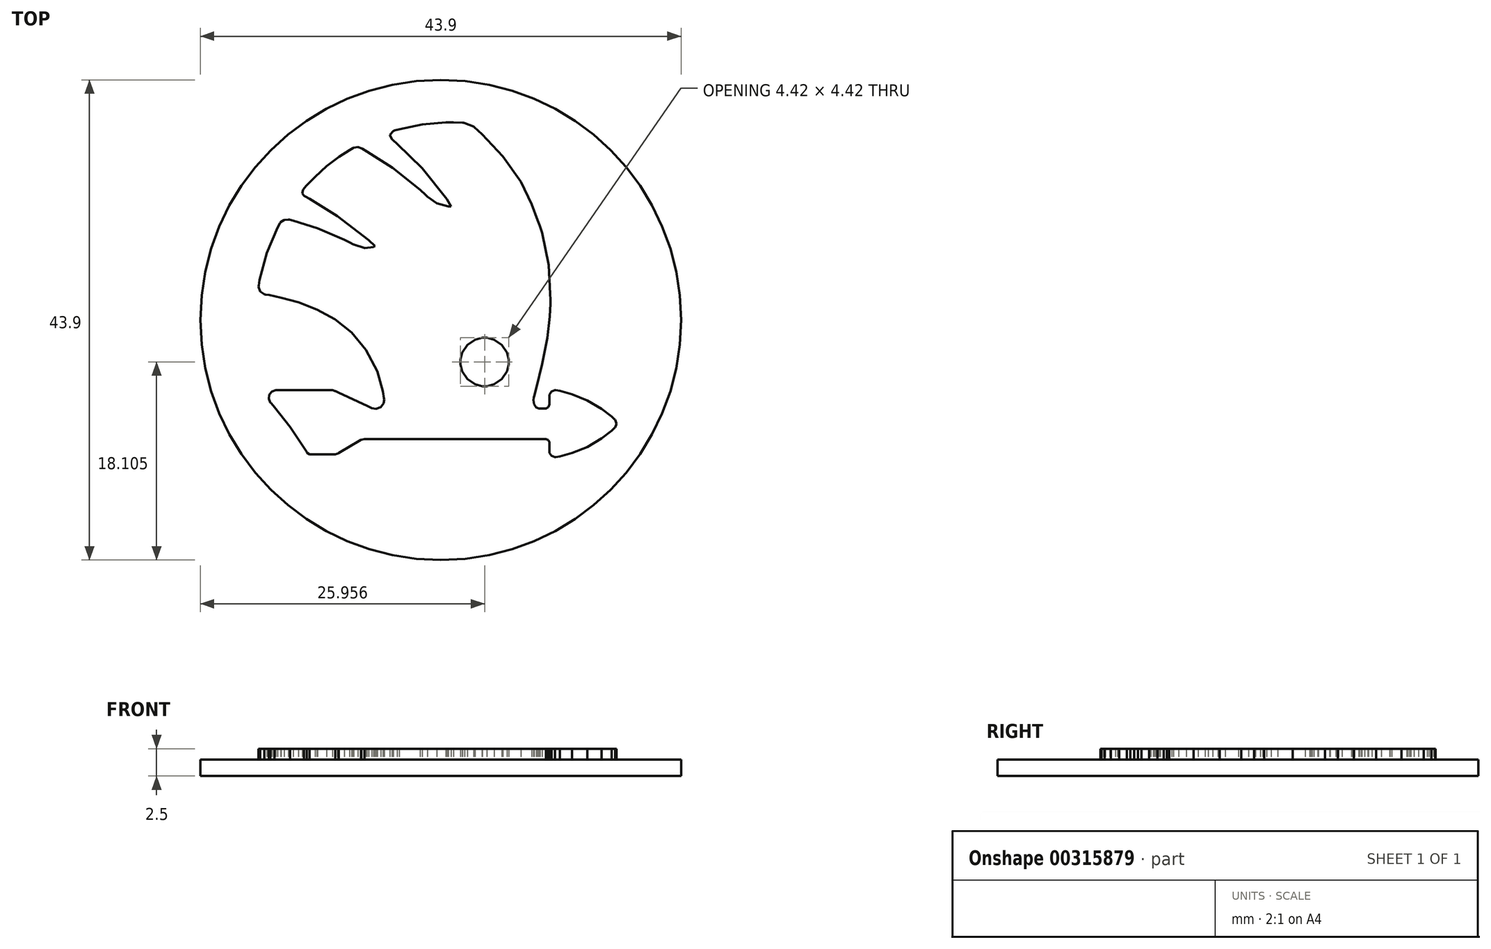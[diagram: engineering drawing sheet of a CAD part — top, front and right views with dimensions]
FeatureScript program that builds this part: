
annotation { "Feature Type Name" : "Feature", "Feature Type Description" : "" }
export const myFeature = defineFeature(function(context is Context, id is Id, definition is map)
    precondition{}
    {
        {
            var Q0;
            Q0=qCreatedBy(makeId("Top.planeOp"),FACE);
            var sketch = newSketch(context, id + "F0", { "sketchPlane" : qUnion([Q0])});
            skCircle(sketch, "E0", {"center": v(0, 0) * mm, "radius": 21.95 * mm});
            skLineSegment(sketch, "E1", {"start": v(15.87, -9.07) * mm, "end": v(15.6, -8.81) * mm});
            skLineSegment(sketch, "E2", {"start": v(15.6, -8.81) * mm, "end": v(14.7, -8.12) * mm});
            skLineSegment(sketch, "E3", {"start": v(14.7, -8.12) * mm, "end": v(13.4, -7.35) * mm});
            skLineSegment(sketch, "E4", {"start": v(13.4, -7.35) * mm, "end": v(11.98, -6.78) * mm});
            skLineSegment(sketch, "E5", {"start": v(11.98, -6.78) * mm, "end": v(10.87, -6.49) * mm});
            skLineSegment(sketch, "E6", {"start": v(10.87, -6.49) * mm, "end": v(10.5, -6.43) * mm});
            skLineSegment(sketch, "E7", {"start": v(10.5, -6.43) * mm, "end": v(10.42, -6.42) * mm});
            skLineSegment(sketch, "E8", {"start": v(10.42, -6.42) * mm, "end": v(10.1, -6.54) * mm});
            skLineSegment(sketch, "E9", {"start": v(10.1, -6.54) * mm, "end": v(9.94, -6.81) * mm});
            skLineSegment(sketch, "E10", {"start": v(9.94, -6.81) * mm, "end": v(9.94, -6.9) * mm});
            skLineSegment(sketch, "E11", {"start": v(9.94, -6.9) * mm, "end": v(9.94, -7.09) * mm});
            skLineSegment(sketch, "E12", {"start": v(9.94, -7.09) * mm, "end": v(9.94, -7.5) * mm});
            skLineSegment(sketch, "E13", {"start": v(9.94, -7.5) * mm, "end": v(9.94, -7.64) * mm});
            skLineSegment(sketch, "E14", {"start": v(9.94, -7.64) * mm, "end": v(9.94, -7.72) * mm});
            skLineSegment(sketch, "E15", {"start": v(9.94, -7.72) * mm, "end": v(9.83, -7.96) * mm});
            skLineSegment(sketch, "E16", {"start": v(9.83, -7.96) * mm, "end": v(9.62, -8.1) * mm});
            skLineSegment(sketch, "E17", {"start": v(9.62, -8.1) * mm, "end": v(9.55, -8.1) * mm});
            skLineSegment(sketch, "E18", {"start": v(9.55, -8.1) * mm, "end": v(9.43, -8.1) * mm});
            skLineSegment(sketch, "E19", {"start": v(9.43, -8.1) * mm, "end": v(9.11, -8.1) * mm});
            skLineSegment(sketch, "E20", {"start": v(9.11, -8.1) * mm, "end": v(9.07, -8.1) * mm});
            skLineSegment(sketch, "E21", {"start": v(9.07, -8.1) * mm, "end": v(8.99, -8.1) * mm});
            skLineSegment(sketch, "E22", {"start": v(8.99, -8.1) * mm, "end": v(8.73, -7.99) * mm});
            skLineSegment(sketch, "E23", {"start": v(8.73, -7.99) * mm, "end": v(8.54, -7.7) * mm});
            skLineSegment(sketch, "E24", {"start": v(8.54, -7.7) * mm, "end": v(8.48, -7.34) * mm});
            skLineSegment(sketch, "E25", {"start": v(8.48, -7.34) * mm, "end": v(8.5, -7.08) * mm});
            skLineSegment(sketch, "E26", {"start": v(8.5, -7.08) * mm, "end": v(8.52, -7) * mm});
            skLineSegment(sketch, "E27", {"start": v(8.52, -7) * mm, "end": v(8.72, -6.26) * mm});
            skLineSegment(sketch, "E28", {"start": v(8.72, -6.26) * mm, "end": v(9.26, -4.05) * mm});
            skLineSegment(sketch, "E29", {"start": v(9.26, -4.05) * mm, "end": v(9.72, -1.64) * mm});
            skLineSegment(sketch, "E30", {"start": v(9.72, -1.64) * mm, "end": v(9.95, 0.3) * mm});
            skLineSegment(sketch, "E31", {"start": v(9.95, 0.3) * mm, "end": v(10, 1.5) * mm});
            skLineSegment(sketch, "E32", {"start": v(10, 1.5) * mm, "end": v(10, 1.89) * mm});
            skLineSegment(sketch, "E33", {"start": v(10, 1.89) * mm, "end": v(10, 2.4) * mm});
            skLineSegment(sketch, "E34", {"start": v(10, 2.4) * mm, "end": v(9.85, 5.02) * mm});
            skLineSegment(sketch, "E35", {"start": v(9.85, 5.02) * mm, "end": v(9.25, 7.96) * mm});
            skLineSegment(sketch, "E36", {"start": v(9.25, 7.96) * mm, "end": v(9.02, 8.63) * mm});
            skLineSegment(sketch, "E37", {"start": v(9.02, 8.63) * mm, "end": v(8.86, 9.12) * mm});
            skLineSegment(sketch, "E38", {"start": v(8.86, 9.12) * mm, "end": v(8.32, 10.58) * mm});
            skLineSegment(sketch, "E39", {"start": v(8.32, 10.58) * mm, "end": v(7.31, 12.64) * mm});
            skLineSegment(sketch, "E40", {"start": v(7.31, 12.64) * mm, "end": v(5.67, 14.94) * mm});
            skLineSegment(sketch, "E41", {"start": v(5.67, 14.94) * mm, "end": v(3.76, 16.98) * mm});
            skLineSegment(sketch, "E42", {"start": v(3.76, 16.98) * mm, "end": v(3.07, 17.6) * mm});
            skLineSegment(sketch, "E43", {"start": v(3.07, 17.6) * mm, "end": v(3, 17.67) * mm});
            skLineSegment(sketch, "E44", {"start": v(3, 17.67) * mm, "end": v(2.2, 18.02) * mm});
            skLineSegment(sketch, "E45", {"start": v(2.2, 18.02) * mm, "end": v(2.1, 18.02) * mm});
            skLineSegment(sketch, "E46", {"start": v(2.1, 18.02) * mm, "end": v(1.99, 18.03) * mm});
            skLineSegment(sketch, "E47", {"start": v(1.99, 18.03) * mm, "end": v(1.17, 18.07) * mm});
            skLineSegment(sketch, "E48", {"start": v(1.17, 18.07) * mm, "end": v(0.9, 18.07) * mm});
            skLineSegment(sketch, "E49", {"start": v(0.9, 18.07) * mm, "end": v(0.46, 18.07) * mm});
            skLineSegment(sketch, "E50", {"start": v(0.46, 18.07) * mm, "end": v(-1.7, 17.88) * mm});
            skLineSegment(sketch, "E51", {"start": v(-1.7, 17.88) * mm, "end": v(-3.8, 17.44) * mm});
            skLineSegment(sketch, "E52", {"start": v(-3.8, 17.44) * mm, "end": v(-4.2, 17.32) * mm});
            skLineSegment(sketch, "E53", {"start": v(-4.2, 17.32) * mm, "end": v(-4.32, 17.28) * mm});
            skLineSegment(sketch, "E54", {"start": v(-4.32, 17.28) * mm, "end": v(-4.64, 16.92) * mm});
            skLineSegment(sketch, "E55", {"start": v(-4.64, 16.92) * mm, "end": v(-4.46, 16.5) * mm});
            skLineSegment(sketch, "E56", {"start": v(-4.46, 16.5) * mm, "end": v(-4.37, 16.43) * mm});
            skLineSegment(sketch, "E57", {"start": v(-4.37, 16.43) * mm, "end": v(-3.97, 16.1) * mm});
            skLineSegment(sketch, "E58", {"start": v(-3.97, 16.1) * mm, "end": v(-1.69, 13.87) * mm});
            skLineSegment(sketch, "E59", {"start": v(-1.69, 13.87) * mm, "end": v(0.55, 11.04) * mm});
            skLineSegment(sketch, "E60", {"start": v(0.55, 11.04) * mm, "end": v(0.93, 10.4) * mm});
            skLineSegment(sketch, "E61", {"start": v(0.93, 10.4) * mm, "end": v(0.69, 10.37) * mm});
            skLineSegment(sketch, "E62", {"start": v(0.69, 10.37) * mm, "end": v(-0.35, 10.66) * mm});
            skLineSegment(sketch, "E63", {"start": v(-0.35, 10.66) * mm, "end": v(-1.22, 11.28) * mm});
            skLineSegment(sketch, "E64", {"start": v(-1.22, 11.28) * mm, "end": v(-1.37, 11.42) * mm});
            skLineSegment(sketch, "E65", {"start": v(-1.37, 11.42) * mm, "end": v(-1.87, 11.9) * mm});
            skLineSegment(sketch, "E66", {"start": v(-1.87, 11.9) * mm, "end": v(-4.39, 13.9) * mm});
            skLineSegment(sketch, "E67", {"start": v(-4.39, 13.9) * mm, "end": v(-6.73, 15.4) * mm});
            skLineSegment(sketch, "E68", {"start": v(-6.73, 15.4) * mm, "end": v(-7.15, 15.64) * mm});
            skLineSegment(sketch, "E69", {"start": v(-7.15, 15.64) * mm, "end": v(-7.22, 15.68) * mm});
            skLineSegment(sketch, "E70", {"start": v(-7.22, 15.68) * mm, "end": v(-7.58, 15.8) * mm});
            skLineSegment(sketch, "E71", {"start": v(-7.58, 15.8) * mm, "end": v(-7.94, 15.75) * mm});
            skLineSegment(sketch, "E72", {"start": v(-7.94, 15.75) * mm, "end": v(-8.01, 15.7) * mm});
            skLineSegment(sketch, "E73", {"start": v(-8.01, 15.7) * mm, "end": v(-8.34, 15.52) * mm});
            skLineSegment(sketch, "E74", {"start": v(-8.34, 15.52) * mm, "end": v(-9.29, 14.9) * mm});
            skLineSegment(sketch, "E75", {"start": v(-9.29, 14.9) * mm, "end": v(-10.42, 14.06) * mm});
            skLineSegment(sketch, "E76", {"start": v(-10.42, 14.06) * mm, "end": v(-11.48, 13.1) * mm});
            skLineSegment(sketch, "E77", {"start": v(-11.48, 13.1) * mm, "end": v(-12.28, 12.24) * mm});
            skLineSegment(sketch, "E78", {"start": v(-12.28, 12.24) * mm, "end": v(-12.54, 11.94) * mm});
            skLineSegment(sketch, "E79", {"start": v(-12.54, 11.94) * mm, "end": v(-12.6, 11.88) * mm});
            skLineSegment(sketch, "E80", {"start": v(-12.6, 11.88) * mm, "end": v(-12.65, 11.56) * mm});
            skLineSegment(sketch, "E81", {"start": v(-12.65, 11.56) * mm, "end": v(-12.45, 11.34) * mm});
            skLineSegment(sketch, "E82", {"start": v(-12.45, 11.34) * mm, "end": v(-12.39, 11.3) * mm});
            skLineSegment(sketch, "E83", {"start": v(-12.39, 11.3) * mm, "end": v(-11.99, 11.1) * mm});
            skLineSegment(sketch, "E84", {"start": v(-11.99, 11.1) * mm, "end": v(-9.46, 9.5) * mm});
            skLineSegment(sketch, "E85", {"start": v(-9.46, 9.5) * mm, "end": v(-6.58, 7.3) * mm});
            skLineSegment(sketch, "E86", {"start": v(-6.58, 7.3) * mm, "end": v(-6, 6.77) * mm});
            skLineSegment(sketch, "E87", {"start": v(-6, 6.77) * mm, "end": v(-6.13, 6.67) * mm});
            skLineSegment(sketch, "E88", {"start": v(-6.13, 6.67) * mm, "end": v(-6.92, 6.56) * mm});
            skLineSegment(sketch, "E89", {"start": v(-6.92, 6.56) * mm, "end": v(-8.02, 6.93) * mm});
            skLineSegment(sketch, "E90", {"start": v(-8.02, 6.93) * mm, "end": v(-8.28, 7.07) * mm});
            skLineSegment(sketch, "E91", {"start": v(-8.28, 7.07) * mm, "end": v(-8.8, 7.34) * mm});
            skLineSegment(sketch, "E92", {"start": v(-8.8, 7.34) * mm, "end": v(-11.27, 8.38) * mm});
            skLineSegment(sketch, "E93", {"start": v(-11.27, 8.38) * mm, "end": v(-13.46, 9.07) * mm});
            skLineSegment(sketch, "E94", {"start": v(-13.46, 9.07) * mm, "end": v(-13.83, 9.16) * mm});
            skLineSegment(sketch, "E95", {"start": v(-13.83, 9.16) * mm, "end": v(-13.92, 9.19) * mm});
            skLineSegment(sketch, "E96", {"start": v(-13.92, 9.19) * mm, "end": v(-14.31, 9.16) * mm});
            skLineSegment(sketch, "E97", {"start": v(-14.31, 9.16) * mm, "end": v(-14.63, 8.94) * mm});
            skLineSegment(sketch, "E98", {"start": v(-14.63, 8.94) * mm, "end": v(-14.67, 8.87) * mm});
            skLineSegment(sketch, "E99", {"start": v(-14.67, 8.87) * mm, "end": v(-14.91, 8.45) * mm});
            skLineSegment(sketch, "E100", {"start": v(-14.91, 8.45) * mm, "end": v(-15.9, 6.14) * mm});
            skLineSegment(sketch, "E101", {"start": v(-15.9, 6.14) * mm, "end": v(-16.54, 3.65) * mm});
            skLineSegment(sketch, "E102", {"start": v(-16.54, 3.65) * mm, "end": v(-16.62, 3.14) * mm});
            skLineSegment(sketch, "E103", {"start": v(-16.62, 3.14) * mm, "end": v(-16.64, 3.04) * mm});
            skLineSegment(sketch, "E104", {"start": v(-16.64, 3.04) * mm, "end": v(-16.5, 2.61) * mm});
            skLineSegment(sketch, "E105", {"start": v(-16.5, 2.61) * mm, "end": v(-16.12, 2.35) * mm});
            skLineSegment(sketch, "E106", {"start": v(-16.12, 2.35) * mm, "end": v(-16.03, 2.33) * mm});
            skLineSegment(sketch, "E107", {"start": v(-16.03, 2.33) * mm, "end": v(-15.67, 2.27) * mm});
            skLineSegment(sketch, "E108", {"start": v(-15.67, 2.27) * mm, "end": v(-14.6, 2.04) * mm});
            skLineSegment(sketch, "E109", {"start": v(-14.6, 2.04) * mm, "end": v(-13, 1.6) * mm});
            skLineSegment(sketch, "E110", {"start": v(-13, 1.6) * mm, "end": v(-11.32, 0.96) * mm});
            skLineSegment(sketch, "E111", {"start": v(-11.32, 0.96) * mm, "end": v(-9.68, 0.06) * mm});
            skLineSegment(sketch, "E112", {"start": v(-9.68, 0.06) * mm, "end": v(-8.14, -1.15) * mm});
            skLineSegment(sketch, "E113", {"start": v(-8.14, -1.15) * mm, "end": v(-6.82, -2.72) * mm});
            skLineSegment(sketch, "E114", {"start": v(-6.82, -2.72) * mm, "end": v(-5.8, -4.71) * mm});
            skLineSegment(sketch, "E115", {"start": v(-5.8, -4.71) * mm, "end": v(-5.28, -6.55) * mm});
            skLineSegment(sketch, "E116", {"start": v(-5.28, -6.55) * mm, "end": v(-5.18, -7.17) * mm});
            skLineSegment(sketch, "E117", {"start": v(-5.18, -7.17) * mm, "end": v(-5.17, -7.28) * mm});
            skLineSegment(sketch, "E118", {"start": v(-5.17, -7.28) * mm, "end": v(-5.23, -7.62) * mm});
            skLineSegment(sketch, "E119", {"start": v(-5.23, -7.62) * mm, "end": v(-5.49, -7.96) * mm});
            skLineSegment(sketch, "E120", {"start": v(-5.49, -7.96) * mm, "end": v(-5.9, -8.11) * mm});
            skLineSegment(sketch, "E121", {"start": v(-5.9, -8.11) * mm, "end": v(-6.31, -8.06) * mm});
            skLineSegment(sketch, "E122", {"start": v(-6.31, -8.06) * mm, "end": v(-6.43, -8) * mm});
            skLineSegment(sketch, "E123", {"start": v(-6.43, -8) * mm, "end": v(-6.7, -7.88) * mm});
            skLineSegment(sketch, "E124", {"start": v(-6.7, -7.88) * mm, "end": v(-9.34, -6.64) * mm});
            skLineSegment(sketch, "E125", {"start": v(-9.34, -6.64) * mm, "end": v(-9.6, -6.52) * mm});
            skLineSegment(sketch, "E126", {"start": v(-9.6, -6.52) * mm, "end": v(-9.63, -6.5) * mm});
            skLineSegment(sketch, "E127", {"start": v(-9.63, -6.5) * mm, "end": v(-9.88, -6.42) * mm});
            skLineSegment(sketch, "E128", {"start": v(-9.88, -6.42) * mm, "end": v(-9.96, -6.42) * mm});
            skLineSegment(sketch, "E129", {"start": v(-9.96, -6.42) * mm, "end": v(-11.2, -6.42) * mm});
            skLineSegment(sketch, "E130", {"start": v(-11.2, -6.42) * mm, "end": v(-14.01, -6.42) * mm});
            skLineSegment(sketch, "E131", {"start": v(-14.01, -6.42) * mm, "end": v(-14.95, -6.42) * mm});
            skLineSegment(sketch, "E132", {"start": v(-14.95, -6.42) * mm, "end": v(-15.06, -6.42) * mm});
            skLineSegment(sketch, "E133", {"start": v(-15.06, -6.42) * mm, "end": v(-15.4, -6.54) * mm});
            skLineSegment(sketch, "E134", {"start": v(-15.4, -6.54) * mm, "end": v(-15.66, -6.83) * mm});
            skLineSegment(sketch, "E135", {"start": v(-15.66, -6.83) * mm, "end": v(-15.7, -7.22) * mm});
            skLineSegment(sketch, "E136", {"start": v(-15.7, -7.22) * mm, "end": v(-15.56, -7.54) * mm});
            skLineSegment(sketch, "E137", {"start": v(-15.56, -7.54) * mm, "end": v(-15.49, -7.63) * mm});
            skLineSegment(sketch, "E138", {"start": v(-15.49, -7.63) * mm, "end": v(-15.19, -7.97) * mm});
            skLineSegment(sketch, "E139", {"start": v(-15.19, -7.97) * mm, "end": v(-13.77, -9.78) * mm});
            skLineSegment(sketch, "E140", {"start": v(-13.77, -9.78) * mm, "end": v(-12.48, -11.68) * mm});
            skLineSegment(sketch, "E141", {"start": v(-12.48, -11.68) * mm, "end": v(-12.25, -12.08) * mm});
            skLineSegment(sketch, "E142", {"start": v(-12.25, -12.08) * mm, "end": v(-12.23, -12.11) * mm});
            skLineSegment(sketch, "E143", {"start": v(-12.23, -12.11) * mm, "end": v(-11.99, -12.27) * mm});
            skLineSegment(sketch, "E144", {"start": v(-11.99, -12.27) * mm, "end": v(-11.9, -12.27) * mm});
            skLineSegment(sketch, "E145", {"start": v(-11.9, -12.27) * mm, "end": v(-11.36, -12.27) * mm});
            skLineSegment(sketch, "E146", {"start": v(-11.36, -12.27) * mm, "end": v(-10.14, -12.27) * mm});
            skLineSegment(sketch, "E147", {"start": v(-10.14, -12.27) * mm, "end": v(-9.73, -12.27) * mm});
            skLineSegment(sketch, "E148", {"start": v(-9.73, -12.27) * mm, "end": v(-9.63, -12.27) * mm});
            skLineSegment(sketch, "E149", {"start": v(-9.63, -12.27) * mm, "end": v(-9.36, -12.18) * mm});
            skLineSegment(sketch, "E150", {"start": v(-9.36, -12.18) * mm, "end": v(-9.33, -12.16) * mm});
            skLineSegment(sketch, "E151", {"start": v(-9.33, -12.16) * mm, "end": v(-9.16, -12.06) * mm});
            skLineSegment(sketch, "E152", {"start": v(-9.16, -12.06) * mm, "end": v(-7.44, -11.06) * mm});
            skLineSegment(sketch, "E153", {"start": v(-7.44, -11.06) * mm, "end": v(-7.27, -10.96) * mm});
            skLineSegment(sketch, "E154", {"start": v(-7.27, -10.96) * mm, "end": v(-7.24, -10.94) * mm});
            skLineSegment(sketch, "E155", {"start": v(-7.24, -10.94) * mm, "end": v(-6.96, -10.89) * mm});
            skLineSegment(sketch, "E156", {"start": v(-6.96, -10.89) * mm, "end": v(-6.87, -10.89) * mm});
            skLineSegment(sketch, "E157", {"start": v(-6.87, -10.89) * mm, "end": v(-2.77, -10.89) * mm});
            skLineSegment(sketch, "E158", {"start": v(-2.77, -10.89) * mm, "end": v(6.46, -10.89) * mm});
            skLineSegment(sketch, "E159", {"start": v(6.46, -10.89) * mm, "end": v(9.54, -10.89) * mm});
            skLineSegment(sketch, "E160", {"start": v(9.54, -10.89) * mm, "end": v(9.61, -10.89) * mm});
            skLineSegment(sketch, "E161", {"start": v(9.61, -10.89) * mm, "end": v(9.82, -10.98) * mm});
            skLineSegment(sketch, "E162", {"start": v(9.82, -10.98) * mm, "end": v(9.94, -11.18) * mm});
            skLineSegment(sketch, "E163", {"start": v(9.94, -11.18) * mm, "end": v(9.94, -11.25) * mm});
            skLineSegment(sketch, "E164", {"start": v(9.94, -11.25) * mm, "end": v(9.94, -11.45) * mm});
            skLineSegment(sketch, "E165", {"start": v(9.94, -11.45) * mm, "end": v(9.94, -11.9) * mm});
            skLineSegment(sketch, "E166", {"start": v(9.94, -11.9) * mm, "end": v(9.94, -12.06) * mm});
            skLineSegment(sketch, "E167", {"start": v(9.94, -12.06) * mm, "end": v(9.94, -12.15) * mm});
            skLineSegment(sketch, "E168", {"start": v(9.94, -12.15) * mm, "end": v(10.1, -12.42) * mm});
            skLineSegment(sketch, "E169", {"start": v(10.1, -12.42) * mm, "end": v(10.42, -12.54) * mm});
            skLineSegment(sketch, "E170", {"start": v(10.42, -12.54) * mm, "end": v(10.5, -12.53) * mm});
            skLineSegment(sketch, "E171", {"start": v(10.5, -12.53) * mm, "end": v(10.87, -12.47) * mm});
            skLineSegment(sketch, "E172", {"start": v(10.87, -12.47) * mm, "end": v(11.98, -12.17) * mm});
            skLineSegment(sketch, "E173", {"start": v(11.98, -12.17) * mm, "end": v(13.4, -11.6) * mm});
            skLineSegment(sketch, "E174", {"start": v(13.4, -11.6) * mm, "end": v(14.7, -10.84) * mm});
            skLineSegment(sketch, "E175", {"start": v(14.7, -10.84) * mm, "end": v(15.6, -10.14) * mm});
            skLineSegment(sketch, "E176", {"start": v(15.6, -10.14) * mm, "end": v(15.87, -9.89) * mm});
            skLineSegment(sketch, "E177", {"start": v(15.87, -9.89) * mm, "end": v(15.93, -9.83) * mm});
            skLineSegment(sketch, "E178", {"start": v(15.93, -9.83) * mm, "end": v(16.05, -9.48) * mm});
            skLineSegment(sketch, "E179", {"start": v(16.05, -9.48) * mm, "end": v(15.93, -9.13) * mm});
            skLineSegment(sketch, "E180", {"start": v(15.93, -9.13) * mm, "end": v(15.87, -9.07) * mm});
            skLineSegment(sketch, "E181", {"start": v(6.22, -3.85) * mm, "end": v(6.22, -4.06) * mm});
            skLineSegment(sketch, "E182", {"start": v(6.22, -4.06) * mm, "end": v(6.04, -4.7) * mm});
            skLineSegment(sketch, "E183", {"start": v(6.04, -4.7) * mm, "end": v(5.57, -5.4) * mm});
            skLineSegment(sketch, "E184", {"start": v(5.57, -5.4) * mm, "end": v(4.87, -5.88) * mm});
            skLineSegment(sketch, "E185", {"start": v(4.87, -5.88) * mm, "end": v(4.22, -6.06) * mm});
            skLineSegment(sketch, "E186", {"start": v(4.22, -6.06) * mm, "end": v(4, -6.06) * mm});
            skLineSegment(sketch, "E187", {"start": v(4, -6.06) * mm, "end": v(3.79, -6.06) * mm});
            skLineSegment(sketch, "E188", {"start": v(3.79, -6.06) * mm, "end": v(3.14, -5.88) * mm});
            skLineSegment(sketch, "E189", {"start": v(3.14, -5.88) * mm, "end": v(2.44, -5.4) * mm});
            skLineSegment(sketch, "E190", {"start": v(2.44, -5.4) * mm, "end": v(1.97, -4.7) * mm});
            skLineSegment(sketch, "E191", {"start": v(1.97, -4.7) * mm, "end": v(1.8, -4.06) * mm});
            skLineSegment(sketch, "E192", {"start": v(1.8, -4.06) * mm, "end": v(1.8, -3.85) * mm});
            skLineSegment(sketch, "E193", {"start": v(1.8, -3.85) * mm, "end": v(1.8, -3.63) * mm});
            skLineSegment(sketch, "E194", {"start": v(1.8, -3.63) * mm, "end": v(1.97, -2.98) * mm});
            skLineSegment(sketch, "E195", {"start": v(1.97, -2.98) * mm, "end": v(2.44, -2.28) * mm});
            skLineSegment(sketch, "E196", {"start": v(2.44, -2.28) * mm, "end": v(3.14, -1.8) * mm});
            skLineSegment(sketch, "E197", {"start": v(3.14, -1.8) * mm, "end": v(3.79, -1.63) * mm});
            skLineSegment(sketch, "E198", {"start": v(3.79, -1.63) * mm, "end": v(4, -1.63) * mm});
            skLineSegment(sketch, "E199", {"start": v(4, -1.63) * mm, "end": v(4.22, -1.63) * mm});
            skLineSegment(sketch, "E200", {"start": v(4.22, -1.63) * mm, "end": v(4.87, -1.8) * mm});
            skLineSegment(sketch, "E201", {"start": v(4.87, -1.8) * mm, "end": v(5.57, -2.28) * mm});
            skLineSegment(sketch, "E202", {"start": v(5.57, -2.28) * mm, "end": v(6.04, -2.98) * mm});
            skLineSegment(sketch, "E203", {"start": v(6.04, -2.98) * mm, "end": v(6.22, -3.63) * mm});
            skLineSegment(sketch, "E204", {"start": v(6.22, -3.63) * mm, "end": v(6.22, -3.85) * mm});
            skSolve(sketch);
        }
        {
            var Q0;
            Q0=makeQuery(id+"F0.imprint","IMPRINT",FACE,{"disambiguationData":[TD([[makeQuery(id+"F0.imprint","IMPRINT",EDGE,{"derivedFrom":sQuery(id+"F0.wireOp",EDGE,"E181")}),-1.0]])]});
            var Q1;
            Q1=makeQuery(id+"F0.imprint","IMPRINT",FACE,{"disambiguationData":[TD([[makeQuery(id+"F0.imprint","IMPRINT",EDGE,{"derivedFrom":sQuery(id+"F0.wireOp",EDGE,"E1")}),1.0]])]});
            var Q2;
            Q2=makeQuery(id+"F0.imprint","IMPRINT",FACE,{"disambiguationData":[TD([[makeQuery(id+"F0.imprint","IMPRINT",EDGE,{"derivedFrom":sQuery(id+"F0.wireOp",EDGE,"E0")}),1.0]])]});
            extrude(context, id + "F1", {"entities" : qUnion([Q0, Q1, Q2]), "oppositeDirection" : true, "depth" : 1.5 * mm});
        }
        {
            var Q0;
            Q0=makeQuery(id+"F0.imprint","IMPRINT",FACE,{"disambiguationData":[TD([[makeQuery(id+"F0.imprint","IMPRINT",EDGE,{"derivedFrom":sQuery(id+"F0.wireOp",EDGE,"E1")}),1.0]])]});
            extrude(context, id + "F2", {"entities" : qUnion([Q0]), "depth" : 1 * mm});
        }
    });
